# Revit family: Фонарный столб Л-03 со светильником Арт 7433
name_source: partatom
category: Антураж
revit_build: Autodesk Revit 2018 (Build: 20180423_1000(x64)
units: mm (PartAtom-declared; Revit-internal decimal feet)

## family parameters
Всегда вертикально = Да
Источник визуального образа = Геометрия семейства
На основе рабочей плоскости = Нет
Общий = Нет
При загрузке вырезать с полостями = Нет
Точка расчета площади = Нет

## types (6) — shared parameters
URL = https://hobbyka.ru
Артикул товара = Арт. 7433
Группа модели = Светильники с чугунными опорами
Длина = 460 мм
Изготовитель = ООО «Хоббика»
Изображение типоразмера = Фонарный столб Л-03 со светильником Арт 7433.jpg
Материал изделия = Сталь, поликарбонат
Цвет основания = Сталь
Цвет столба = Нержавейка
Ширина = 460 мм

## per-type parameters (varying)
| type | Версия 3,195 м | Версия 3,695 м | Версия 4,195 м | Версия 4,695 м | Версия 5,195 м | Высота | Высота столба | Описание |
| Версия 3,195 м | Да | Нет | Нет | Нет | Нет | 3195 мм | 1955 мм | Фонарный столб Л-03 со светильником. Версия 3,195 м |
| Версия 3,695 м | Нет | Да | Нет | Нет | Нет | 3695 мм | 2455 мм | Фонарный столб Л-03 со светильником. Версия 3,695 м |
| Версия 4,195 м | Нет | Нет | Да | Нет | Нет | 4195 мм | 2955 мм | Фонарный столб Л-03 со светильником. Версия 4,195 м |
| Версия 4,695 м | Нет | Нет | Нет | Да | Нет | 4695 мм | 3455 мм | Фонарный столб Л-03 со светильником. Версия 4,695 м |
| Версия 5,195 м | Нет | Нет | Нет | Нет | Да | 5195 мм | 3955 мм | Фонарный столб Л-03 со светильником. Версия 5,195 м |
| Версия 5,695 м | Нет | Нет | Нет | Нет | Нет | 5695 мм | 4455 мм | Фонарный столб Л-03 со светильником. Версия 5,695 м |
